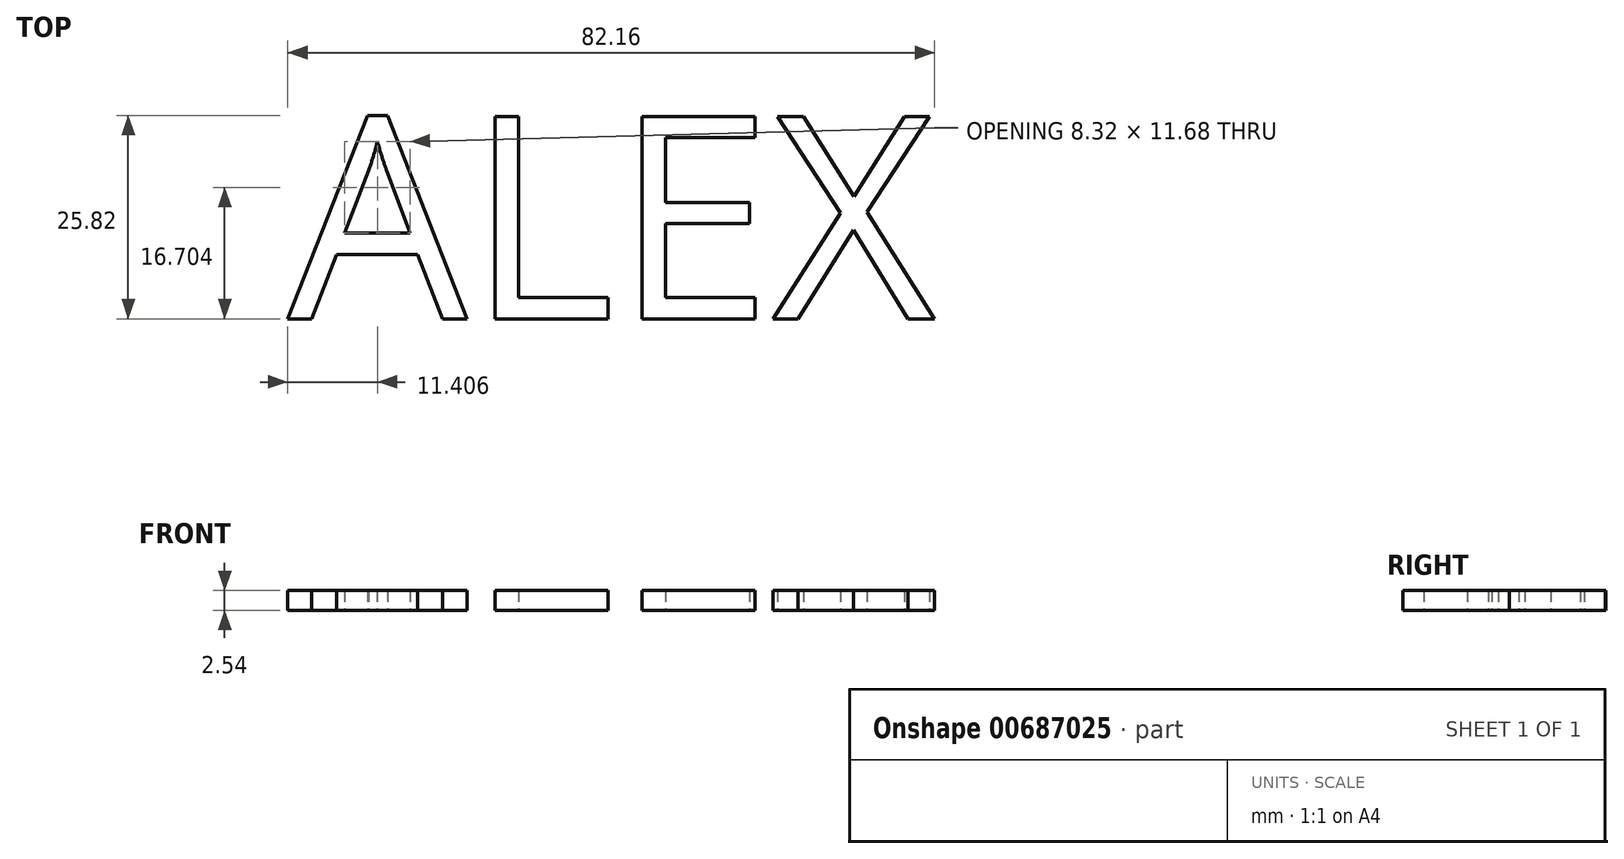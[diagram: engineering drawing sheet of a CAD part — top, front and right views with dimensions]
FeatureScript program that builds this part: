
annotation { "Feature Type Name" : "Feature", "Feature Type Description" : "" }
export const myFeature = defineFeature(function(context is Context, id is Id, definition is map)
    precondition{}
    {
        {
            var Q0;
            Q0=qCreatedBy(makeId("Top.planeOp"),FACE);
            var sketch = newSketch(context, id + "F0", { "sketchPlane" : qUnion([Q0])});
            skText(sketch, "E0", { "text": "ALEX", "fontName": "OpenSans-Regular.ttf"});
            const initialGuessF0  = {"E0": [-0.02365, 0, 1, 0, 0.02593]};
            skSetInitialGuess(sketch, initialGuessF0);
            skSolve(sketch);
        }
        {
            var Q0;
            Q0 = qSketchRegion(id + "F0", true);
            extrude(context, id + "F1", {"entities" : qUnion([Q0]), "depth" : 2.54 * mm, "offsetDistance" : 25.4 * mm});
        }
    });
